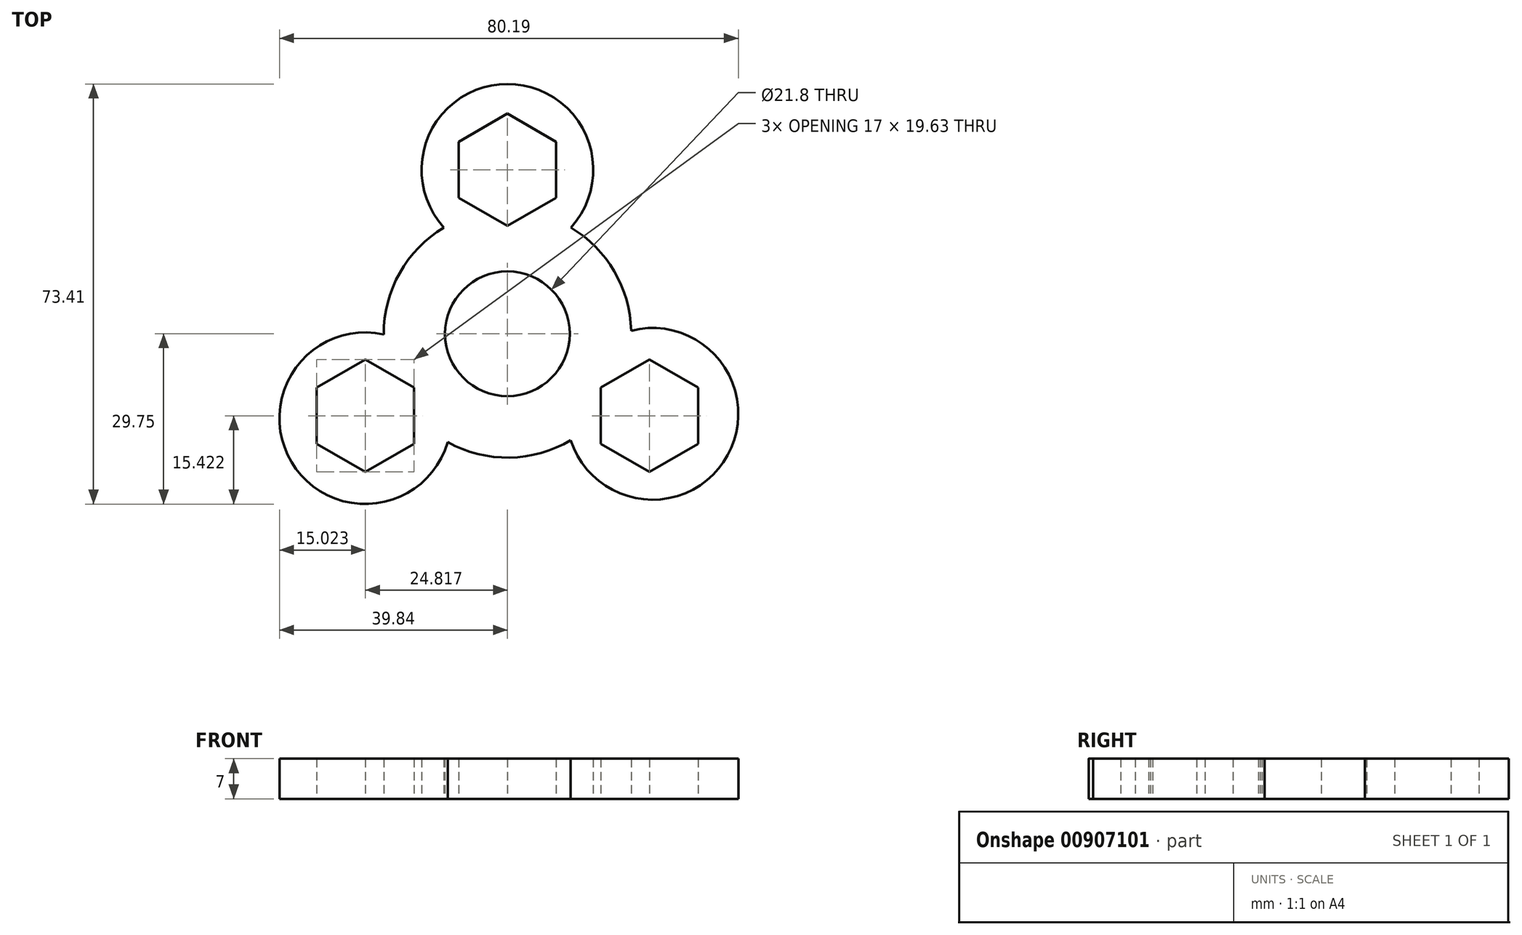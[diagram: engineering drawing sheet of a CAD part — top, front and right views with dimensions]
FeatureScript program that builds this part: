
annotation { "Feature Type Name" : "Feature", "Feature Type Description" : "" }
export const myFeature = defineFeature(function(context is Context, id is Id, definition is map)
    precondition{}
    {
        {
            var Q0;
            Q0=qCreatedBy(makeId("Top.planeOp"),FACE);
            var sketch = newSketch(context, id + "F0", { "sketchPlane" : qUnion([Q0])});
            skCircle(sketch, "E0", {"center": v(0, 0) * mm, "radius": 10.9 * mm});
            skArc(sketch, "E1", {"start": v(11.1, 18.56) * mm, "mid": v(0, 43.66) * mm, "end": v(-11.1, 18.56) * mm});
            skArc(sketch, "E2.1.1", {"start": v(-21.63, -0.1) * mm, "mid": v(-37.74, -22.4) * mm, "end": v(-10.44, -18.94) * mm});
            skArc(sketch, "E2.2.1", {"start": v(11.07, -18.58) * mm, "mid": v(38.48, -21.23) * mm, "end": v(21.62, 0.54) * mm});
            skCircle(sketch, "E3.cCircle", {"center": v(0, 28.66) * mm, "radius": 8.5 * mm, "construction": true});
            skLineSegment(sketch, "E3.0", {"start": v(8.5, 33.56) * mm, "end": v(8.5, 23.75) * mm});
            skLineSegment(sketch, "E3.1", {"start": v(8.5, 23.75) * mm, "end": v(0, 18.84) * mm});
            skLineSegment(sketch, "E3.2", {"start": v(0, 18.84) * mm, "end": v(-8.5, 23.75) * mm});
            skLineSegment(sketch, "E3.3", {"start": v(-8.5, 23.75) * mm, "end": v(-8.5, 33.56) * mm});
            skLineSegment(sketch, "E3.4", {"start": v(-8.5, 33.56) * mm, "end": v(0, 38.47) * mm});
            skLineSegment(sketch, "E3.5", {"start": v(0, 38.47) * mm, "end": v(8.5, 33.56) * mm});
            skPoint(sketch, "E3.0.midPoint", {"position": v(8.5, 28.66) * mm});
            skLineSegment(sketch, "E4.1.0", {"start": v(-24.82, -24.14) * mm, "end": v(-33.32, -19.24) * mm});
            skLineSegment(sketch, "E4.1.1", {"start": v(-33.32, -19.24) * mm, "end": v(-33.32, -9.42) * mm});
            skLineSegment(sketch, "E4.1.2", {"start": v(-33.32, -9.42) * mm, "end": v(-24.82, -4.51) * mm});
            skLineSegment(sketch, "E4.1.3", {"start": v(-24.82, -4.51) * mm, "end": v(-16.32, -9.42) * mm});
            skLineSegment(sketch, "E4.1.4", {"start": v(-16.32, -9.42) * mm, "end": v(-16.32, -19.24) * mm});
            skLineSegment(sketch, "E4.1.5", {"start": v(-16.32, -19.24) * mm, "end": v(-24.82, -24.14) * mm});
            skLineSegment(sketch, "E4.2.0", {"start": v(33.32, -9.42) * mm, "end": v(33.32, -19.24) * mm});
            skLineSegment(sketch, "E4.2.1", {"start": v(33.32, -19.24) * mm, "end": v(24.82, -24.14) * mm});
            skLineSegment(sketch, "E4.2.2", {"start": v(24.82, -24.14) * mm, "end": v(16.32, -19.24) * mm});
            skLineSegment(sketch, "E4.2.3", {"start": v(16.32, -19.24) * mm, "end": v(16.32, -9.42) * mm});
            skLineSegment(sketch, "E4.2.4", {"start": v(16.32, -9.42) * mm, "end": v(24.82, -4.51) * mm});
            skLineSegment(sketch, "E4.2.5", {"start": v(24.82, -4.51) * mm, "end": v(33.32, -9.42) * mm});
            skArc(sketch, "E5", {"start": v(-11.1, 18.56) * mm, "mid": v(-18.83, 10.63) * mm, "end": v(-21.63, -0.1) * mm});
            skArc(sketch, "E6.1.0", {"start": v(-10.44, -18.94) * mm, "mid": v(0.36, -21.62) * mm, "end": v(11.07, -18.58) * mm});
            skArc(sketch, "E6.2.0", {"start": v(21.62, 0.54) * mm, "mid": v(18.68, 10.9) * mm, "end": v(11.1, 18.56) * mm});
            skSolve(sketch);
        }
        {
            var Q0;
            Q0=makeQuery(id+"F0.imprint","IMPRINT",FACE,{"disambiguationData":[TD([[makeQuery(id+"F0.imprint","IMPRINT",EDGE,{"derivedFrom":sQuery(id+"F0.wireOp",EDGE,"E0")}),-1.0]])]});
            extrude(context, id + "F1", {"entities" : qUnion([Q0]), "depth" : 7 * mm, "offsetDistance" : 25 * mm});
        }
    });
